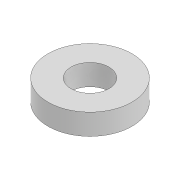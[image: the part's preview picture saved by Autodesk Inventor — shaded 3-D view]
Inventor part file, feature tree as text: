
AUTODESK INVENTOR PART (.ipt)
format: ipt  version: 2022 (Build 260153000, 153)  size: 81,920 bytes
history: native  units: mm
features: extrude x1, sketch x1
ambient origin geometry x8: Origin, YZ Plane, XZ Plane, XY Plane, X Axis, Y Axis, Z Axis, Center Point
bodies: Solid1 (feature_tree)
feature tree (2):
  extrude  "Extrusion1"  Depth=10.0mm
  sketch  "Sketch1"  dims[d0=4.5mm d1=10.0mm d2=2.5mm d3=0.0mm]
